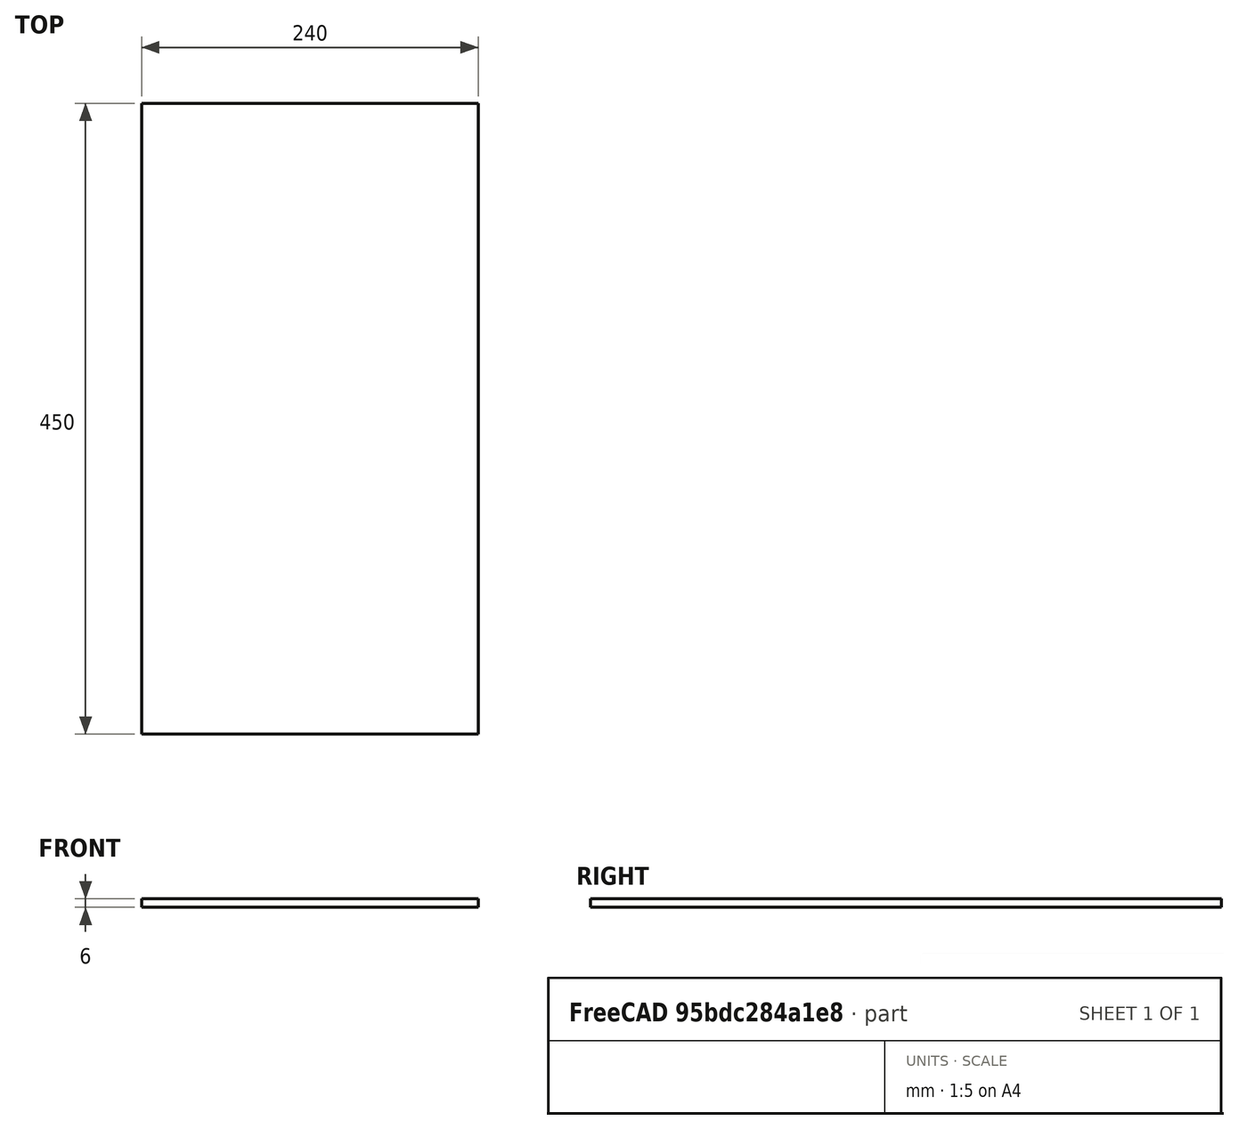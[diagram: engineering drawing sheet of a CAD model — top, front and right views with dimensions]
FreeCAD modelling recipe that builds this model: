
FCSTD DOCUMENT  (FreeCAD 0.18R4 (GitTag))
Label: Gabinete_Base
License: All rights reserved
LicenseURL: http://en.wikipedia.org/wiki/All_rights_reserved
objects: Sketcher::SketchObject×1, PartDesign::Pad×1, PartDesign::Body×1
note: 4 computed .brp shape members not serialized (recipe doc carries the construction recipe); baked Part::Feature solids carry a one-line shape summary decoded from their .brp

FEATURE [Sketcher::SketchObject] Sketch
  MapMode = 5
  Support = -> [XY_Plane]
  sketch-geometry (4):
    g0: LineSegment StartX=0 StartY=0 StartZ=0 EndX=240 EndY=0 EndZ=0
    g1: LineSegment StartX=240 StartY=0 StartZ=0 EndX=240 EndY=450 EndZ=0
    g2: LineSegment StartX=240 StartY=450 StartZ=0 EndX=0 EndY=450 EndZ=0
    g3: LineSegment StartX=0 StartY=450 StartZ=0 EndX=0 EndY=0 EndZ=0
  constraints (11):
    c: Coincident(g0,g1)
    c: Coincident(g1,g2)
    c: Coincident(g2,g3)
    c: Coincident(g3,g0)
    c: Horizontal(g0)
    c: Horizontal(g2)
    c: Vertical(g1)
    c: Vertical(g3)
    c: DistanceX(g0,g0) = 240
    c: DistanceY(g3,g3) = 450
    c: Coincident(g0,g-1)
FEATURE [PartDesign::Pad] Pad
  Length = 6
  Length2 = 100
  Profile = -> Sketch
  Type = 0
FEATURE [PartDesign::Body] Body
  Group = -> [Sketch,Pad]
  Origin = -> Origin
  Tip = -> Pad
